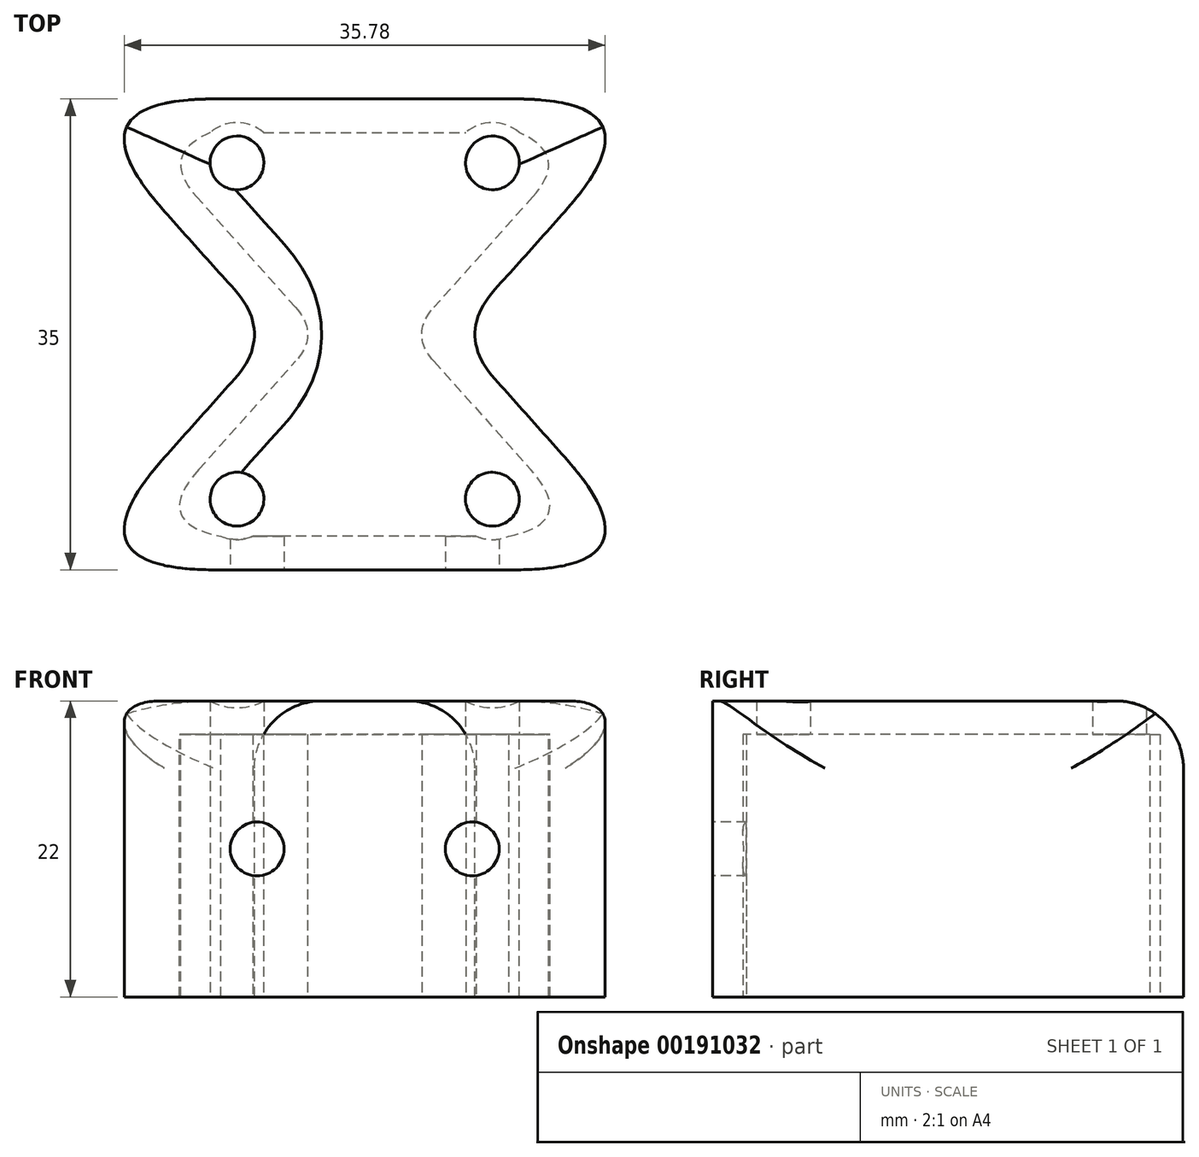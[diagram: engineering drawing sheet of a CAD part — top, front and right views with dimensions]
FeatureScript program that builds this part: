
annotation { "Feature Type Name" : "Feature", "Feature Type Description" : "" }
export const myFeature = defineFeature(function(context is Context, id is Id, definition is map)
    precondition{}
    {
        {
            var Q0;
            Q0=qCreatedBy(makeId("Top.planeOp"),FACE);
            var sketch = newSketch(context, id + "F0", { "sketchPlane" : qUnion([Q0])});
            skCircle(sketch, "E0.cCircle", {"center": v(-22.36, 10) * mm, "radius": 10 * mm, "construction": true});
            skLineSegment(sketch, "E0.0", {"start": v(0, 0) * mm, "end": v(-44.72, 0) * mm});
            skLineSegment(sketch, "E0.1", {"start": v(-44.72, 0) * mm, "end": v(-22.36, 25) * mm});
            skLineSegment(sketch, "E0.2", {"start": v(-22.36, 25) * mm, "end": v(0, 0) * mm});
            skPoint(sketch, "E0.0.midPoint", {"position": v(-22.36, 0) * mm});
            skCircle(sketch, "E1.cCircle", {"center": v(-22.36, 25) * mm, "radius": 10 * mm, "construction": true});
            skLineSegment(sketch, "E1.0", {"start": v(-44.72, 35) * mm, "end": v(0, 35) * mm});
            skLineSegment(sketch, "E1.1", {"start": v(0, 35) * mm, "end": v(-22.36, 10) * mm});
            skLineSegment(sketch, "E1.2", {"start": v(-22.36, 10) * mm, "end": v(-44.72, 35) * mm});
            skPoint(sketch, "E1.0.midPoint", {"position": v(-22.36, 35) * mm});
            skLineSegment(sketch, "E2", {"start": v(-19.38, -6.56) * mm, "end": v(0.94, -6.56) * mm, "construction": true});
            skPoint(sketch, "E3", {"position": v(-31.86, 30.25) * mm});
            skLineSegment(sketch, "E4", {"start": v(-22.36, 35) * mm, "end": v(-22.36, 0) * mm, "construction": true});
            skPoint(sketch, "E5.MirrorP", {"position": v(-12.86, 30.25) * mm});
            skLineSegment(sketch, "E6", {"start": v(-22.36, 17.5) * mm, "end": v(-28.85, 17.75) * mm, "construction": true});
            skLineSegment(sketch, "E7", {"start": v(-28.85, 17.75) * mm, "end": v(-15.43, 17.75) * mm, "construction": true});
            skPoint(sketch, "E8.MirrorP", {"position": v(-31.86, 5.25) * mm});
            skPoint(sketch, "E9.MirrorP", {"position": v(-12.86, 5.25) * mm});
            skSolve(sketch);
        }
        {
            var Q0;
            Q0 = qSketchRegion(id + "F0", true);
            extrude(context, id + "F1", {"entities" : qUnion([Q0]), "depth" : 22 * mm});
        }
        {
            var Q0;
            Q0=makeQuery(id+"F1.opExtrude","CAP_FACE",FACE,{"disambiguationData":[OSD([sQuery(id+"F0.wireOp",EDGE,"E0.0"),sQuery(id+"F0.wireOp",EDGE,"E0.1"),sQuery(id+"F0.wireOp",EDGE,"E0.2"),sQuery(id+"F0.wireOp",EDGE,"E1.0"),sQuery(id+"F0.wireOp",EDGE,"E1.1"),sQuery(id+"F0.wireOp",EDGE,"E1.2")])],"isStart":true});
            shell(context, id + "F2", {"entities" : qUnion([Q0]), "thickness" : 2.5 * mm});
        }
        {
            var Q0;
            Q0=sQuery(id+"F0.wireOp",VERTEX,"E3");
            var Q1;
            Q1=sQuery(id+"F0.wireOp",VERTEX,"E5.MirrorP");
            var Q2;
            Q2=sQuery(id+"F0.wireOp",VERTEX,"E9.MirrorP");
            var Q3;
            Q3=sQuery(id+"F0.wireOp",VERTEX,"E8.MirrorP");
            var Q4;
            Q4=makeQuery(id+"F1.opExtrude","SWEPT_BODY",BODY,{"disambiguationData":[OSD([sQuery(id+"F0.wireOp",EDGE,"E0.0"),sQuery(id+"F0.wireOp",EDGE,"E0.1"),sQuery(id+"F0.wireOp",EDGE,"E0.2"),sQuery(id+"F0.wireOp",EDGE,"E1.0"),sQuery(id+"F0.wireOp",EDGE,"E1.1"),sQuery(id+"F0.wireOp",EDGE,"E1.2")])]});
            hole(context, id + "F3", {"style" : HoleStyle.C_BORE, "endStyle" : HoleEndStyle.BLIND, "oppositeDirection" : true, "holeDiameter" : 4 * mm, "cBoreDiameter" : 6 * mm, "cBoreDepth" : 19.5 * mm, "holeDepth" : 25 * mm, "startFromSketch" : true, "locations" : qUnion([Q0, Q1, Q2, Q3]), "scope" : qUnion([Q4])});
        }
        {
            var Q0;
            Q0=makeQuery(id+"F1.opExtrude","SWEPT_EDGE",EDGE,{"disambiguationData":[OSD([sQuery(id+"F0.wireOp",EDGE,"E0.0"),sQuery(id+"F0.wireOp",EDGE,"E0.1")])]});
            var Q1;
            Q1=makeQuery(id+"F1.opExtrude","SWEPT_EDGE",EDGE,{"disambiguationData":[OSD([sQuery(id+"F0.wireOp",EDGE,"E0.0"),sQuery(id+"F0.wireOp",EDGE,"E0.2")])]});
            var Q2;
            Q2=makeQuery(id+"F1.opExtrude","SWEPT_EDGE",EDGE,{"disambiguationData":[OSD([sQuery(id+"F0.wireOp",EDGE,"E1.0"),sQuery(id+"F0.wireOp",EDGE,"E1.1")])]});
            var Q3;
            Q3=makeQuery(id+"F1.opExtrude","SWEPT_EDGE",EDGE,{"disambiguationData":[OSD([sQuery(id+"F0.wireOp",EDGE,"E1.0"),sQuery(id+"F0.wireOp",EDGE,"E1.2")])]});
            var Q4;
            Q4=makeQuery(id+"F1.opExtrude","SWEPT_EDGE",EDGE,{"disambiguationData":[OSD([sQuery(id+"F0.wireOp",EDGE,"E0.1"),sQuery(id+"F0.wireOp",EDGE,"E1.2")])]});
            var Q5;
            Q5=makeQuery(id+"F1.opExtrude","SWEPT_EDGE",EDGE,{"disambiguationData":[OSD([sQuery(id+"F0.wireOp",EDGE,"E0.2"),sQuery(id+"F0.wireOp",EDGE,"E1.1")])]});
            fillet(context, id + "F4", {"entities" : qUnion([Q0, Q1, Q2, Q3, Q4, Q5]), "radius" : 5 * mm, "tangentPropagation" : true, "rho" : 0.5, "crossSection" : FilletCrossSection.CONIC, "allowEdgeOverflow" : false});
        }
        {
            var Q0;
            Q0=makeQuery(id+"F1.opExtrude","SWEPT_FACE",FACE,{"disambiguationData":[OSD([sQuery(id+"F0.wireOp",EDGE,"E0.0")])]});
            var sketch = newSketch(context, id + "F5", { "sketchPlane" : qUnion([Q0])});
            skLineSegment(sketch, "E10.bottom", {"start": v(-33.54, 22) * mm, "end": v(-11.18, 22) * mm});
            skLineSegment(sketch, "E10.top", {"start": v(-33.54, 0) * mm, "end": v(-11.18, 0) * mm});
            skLineSegment(sketch, "E10.left", {"start": v(-33.54, 22) * mm, "end": v(-33.54, 0) * mm});
            skLineSegment(sketch, "E10.right", {"start": v(-11.18, 22) * mm, "end": v(-11.18, 0) * mm});
            skLineSegment(sketch, "E11", {"start": v(-22.36, 22) * mm, "end": v(-22.36, 0) * mm, "construction": true});
            skLineSegment(sketch, "E12", {"start": v(-33.54, 11) * mm, "end": v(-11.18, 11) * mm, "construction": true});
            skPoint(sketch, "E13", {"position": v(-30.36, 11) * mm});
            skPoint(sketch, "E14.MirrorP", {"position": v(-14.36, 11) * mm});
            skSolve(sketch);
        }
        {
            var Q0;
            Q0=sQuery(id+"F5.wireOp",VERTEX,"E13");
            var Q1;
            Q1=sQuery(id+"F5.wireOp",VERTEX,"E14.MirrorP");
            var Q2;
            Q2=makeQuery(id+"F1.opExtrude","SWEPT_BODY",BODY,{"disambiguationData":[OSD([sQuery(id+"F0.wireOp",EDGE,"E0.0"),sQuery(id+"F0.wireOp",EDGE,"E0.1"),sQuery(id+"F0.wireOp",EDGE,"E0.2"),sQuery(id+"F0.wireOp",EDGE,"E1.0"),sQuery(id+"F0.wireOp",EDGE,"E1.1"),sQuery(id+"F0.wireOp",EDGE,"E1.2")])]});
            hole(context, id + "F6", {"style" : HoleStyle.SIMPLE, "endStyle" : HoleEndStyle.BLIND, "holeDiameter" : 4 * mm, "holeDepth" : 6 * mm, "locations" : qUnion([Q0, Q1]), "scope" : qUnion([Q2])});
        }
        {
            var Q0;
            {var subQ0=sQuery(id+"F0.wireOp",EDGE,"E1.2");var subQ1=sQuery(id+"F0.wireOp",EDGE,"E0.1");Q0=makeQuery(id+"F4.opFillet","BLEND_EDGE",EDGE,{"blendedFrom":[makeQuery(id+"F1.opExtrude","SWEPT_EDGE",EDGE,{"disambiguationData":[OSD([subQ1,subQ0])]}),makeQuery(id+"F1.opExtrude","CAP_FACE",FACE,{"disambiguationData":[OSD([sQuery(id+"F0.wireOp",EDGE,"E0.0"),subQ1,sQuery(id+"F0.wireOp",EDGE,"E0.2"),sQuery(id+"F0.wireOp",EDGE,"E1.0"),sQuery(id+"F0.wireOp",EDGE,"E1.1"),subQ0])],"isStart":false})],"blendedInto":[makeQuery(id+"F1.opExtrude","CAP_FACE",FACE,{"disambiguationData":[OSD([sQuery(id+"F0.wireOp",EDGE,"E0.0"),subQ1,sQuery(id+"F0.wireOp",EDGE,"E0.2"),sQuery(id+"F0.wireOp",EDGE,"E1.0"),sQuery(id+"F0.wireOp",EDGE,"E1.1"),subQ0])],"isStart":false})]});}
            var Q1;
            {var subQ0=sQuery(id+"F0.wireOp",EDGE,"E1.1");var subQ1=sQuery(id+"F0.wireOp",EDGE,"E0.2");Q1=makeQuery(id+"F4.opFillet","BLEND_EDGE",EDGE,{"blendedFrom":[makeQuery(id+"F1.opExtrude","SWEPT_EDGE",EDGE,{"disambiguationData":[OSD([subQ1,subQ0])]}),makeQuery(id+"F1.opExtrude","CAP_FACE",FACE,{"disambiguationData":[OSD([sQuery(id+"F0.wireOp",EDGE,"E0.0"),sQuery(id+"F0.wireOp",EDGE,"E0.1"),subQ1,sQuery(id+"F0.wireOp",EDGE,"E1.0"),subQ0,sQuery(id+"F0.wireOp",EDGE,"E1.2")])],"isStart":false})],"blendedInto":[makeQuery(id+"F1.opExtrude","CAP_FACE",FACE,{"disambiguationData":[OSD([sQuery(id+"F0.wireOp",EDGE,"E0.0"),sQuery(id+"F0.wireOp",EDGE,"E0.1"),subQ1,sQuery(id+"F0.wireOp",EDGE,"E1.0"),subQ0,sQuery(id+"F0.wireOp",EDGE,"E1.2")])],"isStart":false})]});}
            var Q2;
            Q2=makeQuery(id+"F1.opExtrude","CAP_EDGE",EDGE,{"disambiguationData":[OSD([sQuery(id+"F0.wireOp",EDGE,"E1.0")])],"isStart":false});
            fillet(context, id + "F7", {"entities" : qUnion([Q0, Q1, Q2]), "radius" : 5 * mm, "allowEdgeOverflow" : false});
        }
        {
            var Q0;
            Q0=makeQuery(id+"F2.opShell","OFFSET_EDGE",EDGE,{"disambiguationData":[OSD([sQuery(id+"F0.wireOp",EDGE,"E0.0"),sQuery(id+"F0.wireOp",EDGE,"E0.1")])]});
            var Q1;
            Q1=makeQuery(id+"F2.opShell","OFFSET_EDGE",EDGE,{"disambiguationData":[OSD([sQuery(id+"F0.wireOp",EDGE,"E1.0"),sQuery(id+"F0.wireOp",EDGE,"E1.2")])]});
            var Q2;
            Q2=makeQuery(id+"F2.opShell","OFFSET_EDGE",EDGE,{"disambiguationData":[OSD([sQuery(id+"F0.wireOp",EDGE,"E1.0"),sQuery(id+"F0.wireOp",EDGE,"E1.1")])]});
            var Q3;
            Q3=makeQuery(id+"F2.opShell","OFFSET_EDGE",EDGE,{"disambiguationData":[OSD([sQuery(id+"F0.wireOp",EDGE,"E0.0"),sQuery(id+"F0.wireOp",EDGE,"E0.2")])]});
            var Q4;
            Q4=makeQuery(id+"F2.opShell","OFFSET_EDGE",EDGE,{"disambiguationData":[OSD([sQuery(id+"F0.wireOp",EDGE,"E0.1"),sQuery(id+"F0.wireOp",EDGE,"E1.2")])]});
            var Q5;
            Q5=makeQuery(id+"F2.opShell","OFFSET_EDGE",EDGE,{"disambiguationData":[OSD([sQuery(id+"F0.wireOp",EDGE,"E0.2"),sQuery(id+"F0.wireOp",EDGE,"E1.1")])]});
            fillet(context, id + "F8", {"entities" : qUnion([Q0, Q1, Q2, Q3, Q4, Q5]), "radius" : 3 * mm, "tangentPropagation" : true, "rho" : 0.5, "crossSection" : FilletCrossSection.CONIC, "allowEdgeOverflow" : false});
        }
    });
